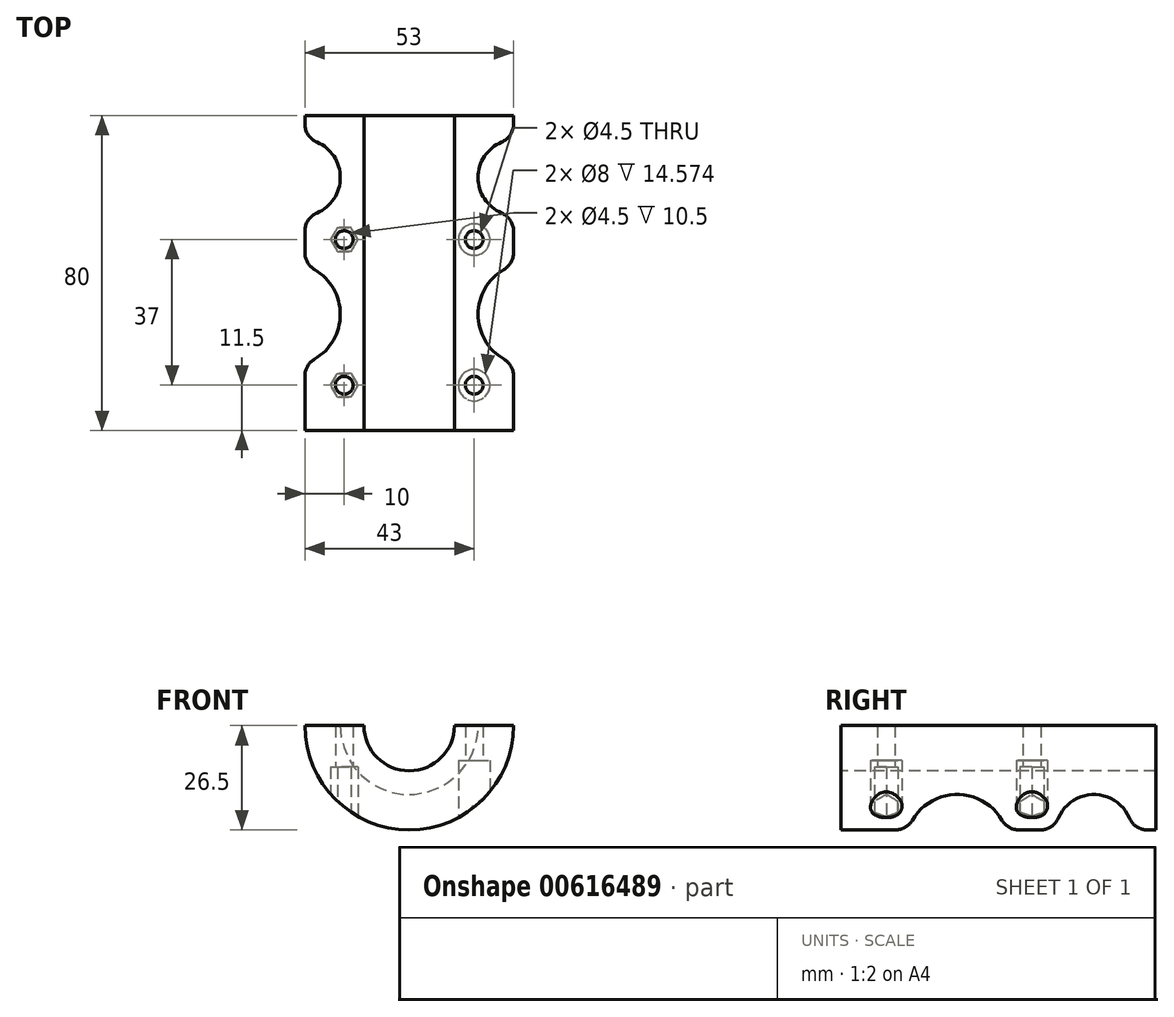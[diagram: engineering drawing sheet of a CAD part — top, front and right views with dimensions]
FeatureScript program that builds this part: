
annotation { "Feature Type Name" : "Feature", "Feature Type Description" : "" }
export const myFeature = defineFeature(function(context is Context, id is Id, definition is map)
    precondition{}
    {
        {
            var Q0;
            Q0=qCreatedBy(makeId("Top.planeOp"),FACE);
            var sketch = newSketch(context, id + "F0", { "sketchPlane" : qUnion([Q0])});
            skLineSegment(sketch, "E0.bottom", {"start": v(11.5, 0) * mm, "end": v(26.5, 0) * mm});
            skLineSegment(sketch, "E0.top", {"start": v(11.5, 80) * mm, "end": v(26.5, 80) * mm});
            skLineSegment(sketch, "E0.left", {"start": v(11.5, 0) * mm, "end": v(11.5, 80) * mm});
            skLineSegment(sketch, "E0.right", {"start": v(26.5, 0) * mm, "end": v(26.5, 13.8) * mm});
            skLineSegment(sketch, "E1", {"start": v(0, 0) * mm, "end": v(0, 100) * mm, "construction": true});
            skPoint(sketch, "E2", {"position": v(26.5, 17) * mm});
            skPoint(sketch, "E3", {"position": v(26.5, 42) * mm});
            skPoint(sketch, "E4", {"position": v(26.5, 54.5) * mm});
            skArc(sketch, "E5", {"start": v(24.02, 40.88) * mm, "mid": v(17.5, 29.5) * mm, "end": v(24.02, 18.12) * mm});
            skPoint(sketch, "E6", {"position": v(26.5, 74) * mm});
            skArc(sketch, "E7", {"start": v(23.46, 73.25) * mm, "mid": v(17.5, 64.25) * mm, "end": v(23.46, 55.25) * mm});
            skLineSegment(sketch, "E8.trimOffspring", {"start": v(26.5, 77.85) * mm, "end": v(26.5, 80) * mm});
            skLineSegment(sketch, "E9.trimOffspring", {"start": v(26.5, 45.2) * mm, "end": v(26.5, 50.65) * mm});
            skArc(sketch, "E10.filletArc", {"start": v(26.5, 13.8) * mm, "mid": v(25.84, 16.3) * mm, "end": v(24.02, 18.12) * mm});
            skArc(sketch, "E11.filletArc", {"start": v(24.02, 40.88) * mm, "mid": v(25.84, 42.7) * mm, "end": v(26.5, 45.2) * mm});
            skArc(sketch, "E12.filletArc", {"start": v(26.5, 50.65) * mm, "mid": v(25.67, 53.4) * mm, "end": v(23.46, 55.25) * mm});
            skArc(sketch, "E13.filletArc", {"start": v(23.46, 73.25) * mm, "mid": v(25.67, 75.1) * mm, "end": v(26.5, 77.85) * mm});
            skSolve(sketch);
        }
        {
            var Q0;
            Q0=makeQuery(id+"F0.imprint","IMPRINT",FACE,{"disambiguationData":[TD([[makeQuery(id+"F0.imprint","IMPRINT",EDGE,{"derivedFrom":sQuery(id+"F0.wireOp",EDGE,"E0.bottom")}),1.0]])]});
            var Q1;
            Q1=sQuery(id+"F0.wireOp",EDGE,"E1");
            revolve(context, id + "F1", {"entities" : qUnion([Q0]), "axis" : qUnion([Q1]), "revolveType" : RevolveType.ONE_DIRECTION, "angle" : 180 * degree});
        }
        {
            var Q0;
            Q0=qCreatedBy(makeId("Top.planeOp"),FACE);
            cPlane(context, id + "F2", {"entities" : qUnion([Q0]), "cplaneType" : CPlaneType.OFFSET, "offset" : 26.5 * mm, "oppositeDirection" : true, "width" : 150 * mm, "height" : 150 * mm});
        }
        {
            var Q0;
            Q0=qCreatedBy(id+"F2.planeOp",FACE);
            var sketch = newSketch(context, id + "F3", { "sketchPlane" : qUnion([Q0])});
            skLineSegment(sketch, "E14", {"start": v(0, 0) * mm, "end": v(0, 85.56) * mm, "construction": true});
            skLineSegment(sketch, "E15", {"start": v(27.46, 11.5) * mm, "end": v(-26.4, 11.5) * mm, "construction": true});
            skLineSegment(sketch, "E16", {"start": v(-26.4, 11.5) * mm, "end": v(-6.6, 11.5) * mm, "construction": true});
            skLineSegment(sketch, "E17", {"start": v(26.1, 30) * mm, "end": v(-30.49, 30) * mm, "construction": true});
            skLineSegment(sketch, "E18", {"start": v(-16.5, 11.5) * mm, "end": v(-16.5, 52.13) * mm, "construction": true});
            skLineSegment(sketch, "E19.MirrorCS", {"start": v(16.5, 11.5) * mm, "end": v(16.5, 52.13) * mm, "construction": true});
            skLineSegment(sketch, "E20.MirrorCS", {"start": v(27.46, 48.5) * mm, "end": v(-26.4, 48.5) * mm, "construction": true});
            skPoint(sketch, "E21", {"position": v(16.5, 48.5) * mm});
            skPoint(sketch, "E22.MirrorP", {"position": v(-16.5, 48.5) * mm});
            skCircle(sketch, "E23.cCircle", {"center": v(-16.5, 11.5) * mm, "radius": 3 * mm, "construction": true});
            skLineSegment(sketch, "E23.0", {"start": v(-18.23, 14.5) * mm, "end": v(-14.77, 14.5) * mm});
            skLineSegment(sketch, "E23.1", {"start": v(-14.77, 14.5) * mm, "end": v(-13.04, 11.5) * mm});
            skLineSegment(sketch, "E23.2", {"start": v(-13.04, 11.5) * mm, "end": v(-14.77, 8.5) * mm});
            skLineSegment(sketch, "E23.3", {"start": v(-14.77, 8.5) * mm, "end": v(-18.23, 8.5) * mm});
            skLineSegment(sketch, "E23.4", {"start": v(-18.23, 8.5) * mm, "end": v(-19.96, 11.5) * mm});
            skLineSegment(sketch, "E23.5", {"start": v(-19.96, 11.5) * mm, "end": v(-18.23, 14.5) * mm});
            skPoint(sketch, "E23.0.midPoint", {"position": v(-16.5, 14.5) * mm});
            skLineSegment(sketch, "E24.MirrorCS", {"start": v(-18.23, 45.5) * mm, "end": v(-14.77, 45.5) * mm});
            skLineSegment(sketch, "E25.MirrorCS", {"start": v(-14.77, 45.5) * mm, "end": v(-13.04, 48.5) * mm});
            skCircle(sketch, "E26.MirrorC", {"center": v(-16.5, 48.5) * mm, "radius": 3 * mm, "construction": true});
            skLineSegment(sketch, "E27.MirrorCS", {"start": v(-13.04, 48.5) * mm, "end": v(-14.77, 51.5) * mm});
            skLineSegment(sketch, "E28.MirrorCS", {"start": v(-14.77, 51.5) * mm, "end": v(-18.23, 51.5) * mm});
            skLineSegment(sketch, "E29.MirrorCS", {"start": v(-18.23, 51.5) * mm, "end": v(-19.96, 48.5) * mm});
            skLineSegment(sketch, "E30.MirrorCS", {"start": v(-19.96, 48.5) * mm, "end": v(-18.23, 45.5) * mm});
            skSolve(sketch);
        }
        {
            var Q0;
            Q0=sQuery(id+"F3.wireOp",VERTEX,"E19.MirrorCS.start");
            var Q1;
            Q1=sQuery(id+"F3.wireOp",VERTEX,"E21");
            var Q2;
            Q2=makeQuery(id+"F1.opRevolve","SWEPT_BODY",BODY,{"disambiguationData":[OSD([sQuery(id+"F0.wireOp",EDGE,"E0.bottom"),sQuery(id+"F0.wireOp",EDGE,"E0.top"),sQuery(id+"F0.wireOp",EDGE,"E0.left"),sQuery(id+"F0.wireOp",EDGE,"E0.right"),sQuery(id+"F0.wireOp",EDGE,"E5"),sQuery(id+"F0.wireOp",EDGE,"E7"),sQuery(id+"F0.wireOp",EDGE,"E8.trimOffspring"),sQuery(id+"F0.wireOp",EDGE,"E9.trimOffspring"),sQuery(id+"F0.wireOp",EDGE,"E10.filletArc"),sQuery(id+"F0.wireOp",EDGE,"E11.filletArc"),sQuery(id+"F0.wireOp",EDGE,"E12.filletArc"),sQuery(id+"F0.wireOp",EDGE,"E13.filletArc")])]});
            hole(context, id + "F4", {"style" : HoleStyle.C_BORE, "endStyle" : HoleEndStyle.THROUGH, "oppositeDirection" : true, "holeDiameter" : 4.5 * mm, "cBoreDiameter" : 8 * mm, "cBoreDepth" : 8 * mm, "majorDiameter" : 5 * mm, "isTappedThrough" : true, "tappedDepth" : 12 * mm, "tapClearance" : 3, "locations" : qUnion([Q0, Q1]), "scope" : qUnion([Q2])});
        }
        {
            var Q0;
            Q0=sQuery(id+"F3.wireOp",VERTEX,"E22.MirrorP");
            var Q1;
            Q1=sQuery(id+"F3.wireOp",VERTEX,"E18.start");
            var Q2;
            Q2=makeQuery(id+"F1.opRevolve","SWEPT_BODY",BODY,{"disambiguationData":[OSD([sQuery(id+"F0.wireOp",EDGE,"E0.bottom"),sQuery(id+"F0.wireOp",EDGE,"E0.top"),sQuery(id+"F0.wireOp",EDGE,"E0.left"),sQuery(id+"F0.wireOp",EDGE,"E0.right"),sQuery(id+"F0.wireOp",EDGE,"E5"),sQuery(id+"F0.wireOp",EDGE,"E7"),sQuery(id+"F0.wireOp",EDGE,"E8.trimOffspring"),sQuery(id+"F0.wireOp",EDGE,"E9.trimOffspring"),sQuery(id+"F0.wireOp",EDGE,"E10.filletArc"),sQuery(id+"F0.wireOp",EDGE,"E11.filletArc"),sQuery(id+"F0.wireOp",EDGE,"E12.filletArc"),sQuery(id+"F0.wireOp",EDGE,"E13.filletArc")])]});
            hole(context, id + "F5", {"style" : HoleStyle.SIMPLE, "endStyle" : HoleEndStyle.THROUGH, "oppositeDirection" : true, "holeDiameter" : 4.5 * mm, "majorDiameter" : 5 * mm, "isTappedThrough" : true, "tappedDepth" : 12 * mm, "tapClearance" : 3, "locations" : qUnion([Q0, Q1]), "scope" : qUnion([Q2])});
        }
        {
            var Q0;
            Q0=makeQuery(id+"F3.imprint","IMPRINT",FACE,{"disambiguationData":[TD([[makeQuery(id+"F3.imprint","IMPRINT",EDGE,{"derivedFrom":sQuery(id+"F3.wireOp",EDGE,"E23.0")}),-1.0]])]});
            extrude(context, id + "F6", {"entities" : qUnion([Q0]), "operationType" : NewBodyOperationType.REMOVE, "depth" : 16 * mm, "offsetDistance" : 25 * mm});
        }
        {
            var Q0;
            Q0=makeQuery(id+"F3.imprint","IMPRINT",FACE,{"disambiguationData":[TD([[makeQuery(id+"F3.imprint","IMPRINT",EDGE,{"derivedFrom":sQuery(id+"F3.wireOp",EDGE,"E24.MirrorCS")}),1.0]])]});
            extrude(context, id + "F7", {"entities" : qUnion([Q0]), "operationType" : NewBodyOperationType.REMOVE, "depth" : 16 * mm, "offsetDistance" : 25 * mm});
        }
    });
